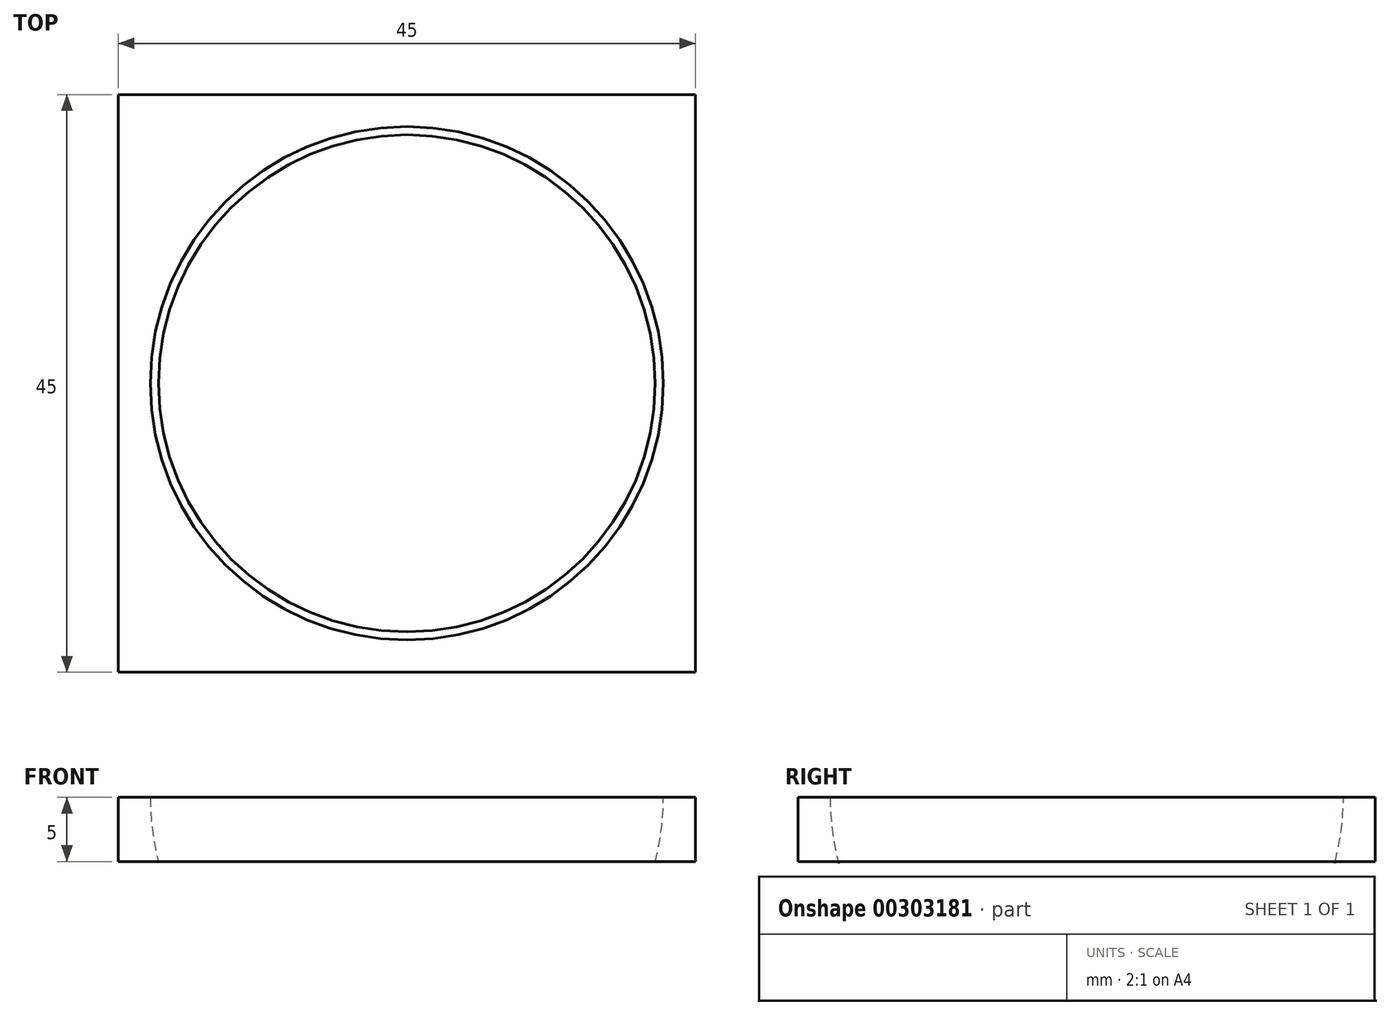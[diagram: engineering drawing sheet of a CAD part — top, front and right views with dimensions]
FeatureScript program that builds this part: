
annotation { "Feature Type Name" : "Feature", "Feature Type Description" : "" }
export const myFeature = defineFeature(function(context is Context, id is Id, definition is map)
    precondition{}
    {
        {
            var Q0;
            Q0=qCreatedBy(makeId("Top.planeOp"),FACE);
            var sketch = newSketch(context, id + "F0", { "sketchPlane" : qUnion([Q0])});
            skLineSegment(sketch, "E0.bottom", {"start": v(22.5, -22.5) * mm, "end": v(-22.5, -22.5) * mm});
            skLineSegment(sketch, "E0.top", {"start": v(22.5, 22.5) * mm, "end": v(-22.5, 22.5) * mm});
            skLineSegment(sketch, "E0.left", {"start": v(22.5, -22.5) * mm, "end": v(22.5, 22.5) * mm});
            skLineSegment(sketch, "E0.right", {"start": v(-22.5, -22.5) * mm, "end": v(-22.5, 22.5) * mm});
            skPoint(sketch, "E0.middle", {"position": v(0, 0) * mm});
            skSolve(sketch);
        }
        {
            var Q0;
            Q0=makeQuery(id+"F0.imprint","IMPRINT",FACE,{"disambiguationData":[TD([[makeQuery(id+"F0.imprint","IMPRINT",EDGE,{"derivedFrom":sQuery(id+"F0.wireOp",EDGE,"E0.bottom")}),-1.0]])]});
            extrude(context, id + "F1", {"entities" : qUnion([Q0]), "oppositeDirection" : true, "depth" : 5 * mm});
        }
        {
            var Q0;
            Q0=makeQuery(id+"F1.opExtrude","CAP_FACE",FACE,{"disambiguationData":[OSD([sQuery(id+"F0.wireOp",EDGE,"E0.bottom"),sQuery(id+"F0.wireOp",EDGE,"E0.top"),sQuery(id+"F0.wireOp",EDGE,"E0.left"),sQuery(id+"F0.wireOp",EDGE,"E0.right")])],"isStart":true});
            var sketch = newSketch(context, id + "F2", { "sketchPlane" : qUnion([Q0])});
            skArc(sketch, "E1", {"start": v(0, -20) * mm, "mid": v(20, 0) * mm, "end": v(0, 20) * mm});
            skLineSegment(sketch, "E2", {"start": v(0, 20) * mm, "end": v(0, -20) * mm});
            skSolve(sketch);
        }
        {
            var Q0;
            Q0=makeQuery(id+"F2.imprint","IMPRINT",FACE,{"disambiguationData":[TD([[makeQuery(id+"F2.imprint","IMPRINT",EDGE,{"derivedFrom":sQuery(id+"F2.wireOp",EDGE,"E1")}),1.0]])]});
            var Q1;
            Q1=sQuery(id+"F2.wireOp",EDGE,"E2");
            revolve(context, id + "F3", {"operationType" : NewBodyOperationType.REMOVE, "entities" : qUnion([Q0]), "axis" : qUnion([Q1]), "revolveType" : RevolveType.FULL, "oppositeDirection" : true});
        }
        {
            var Q0;
            Q0=makeQuery(id+"F2.imprint","IMPRINT",FACE,{"disambiguationData":[TD([[makeQuery(id+"F2.imprint","IMPRINT",EDGE,{"derivedFrom":sQuery(id+"F2.wireOp",EDGE,"E1")}),1.0]])]});
            var Q1;
            Q1=sQuery(id+"F2.wireOp",EDGE,"E2");
            revolve(context, id + "F4", {"operationType" : NewBodyOperationType.REMOVE, "entities" : qUnion([Q0]), "axis" : qUnion([Q1]), "revolveType" : RevolveType.FULL, "oppositeDirection" : true});
        }
    });
